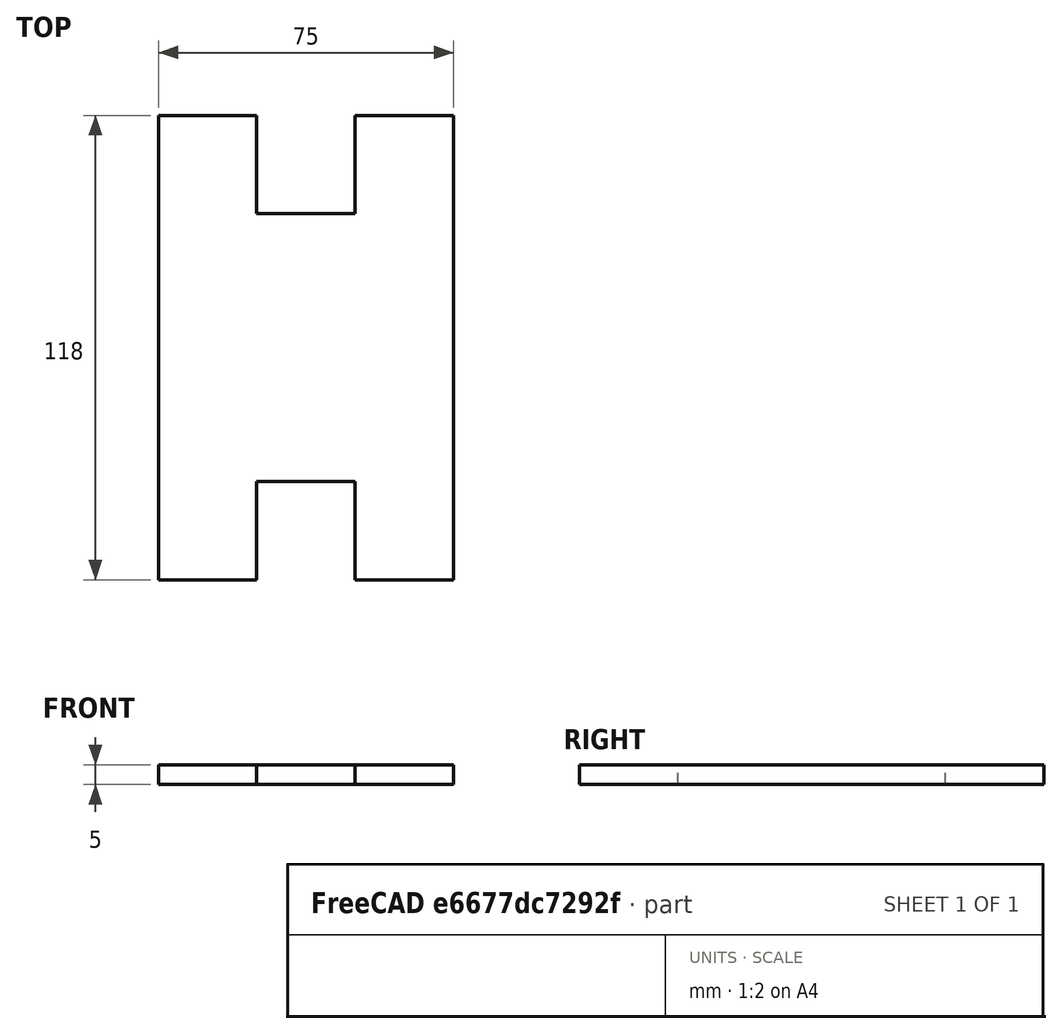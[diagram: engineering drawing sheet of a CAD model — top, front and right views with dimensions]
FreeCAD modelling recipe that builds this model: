
FCSTD DOCUMENT  (FreeCAD 0.16R5231 (Git))
Label: StepperBase
License: All rights reserved
LicenseURL: http://de.wikipedia.org/wiki/Alle_Rechte_vorbehalten
objects: Sketcher::SketchObject×1, PartDesign::Pad×1
note: 3 computed .brp shape members not serialized (recipe doc carries the construction recipe); baked Part::Feature solids carry a one-line shape summary decoded from their .brp

FEATURE [Sketcher::SketchObject] Sketch
  sketch-geometry (15):
    g0: LineSegment StartX=0 StartY=0 StartZ=0 EndX=25 EndY=0 EndZ=0
    g1: LineSegment StartX=25 StartY=0 StartZ=0 EndX=25 EndY=25 EndZ=0
    g2: LineSegment StartX=25 StartY=25 StartZ=0 EndX=50 EndY=25 EndZ=0
    g3: LineSegment StartX=50 StartY=25 StartZ=0 EndX=50 EndY=0 EndZ=0
    g4: LineSegment StartX=50 StartY=0 StartZ=0 EndX=75 EndY=0 EndZ=0
    g5: LineSegment StartX=75 StartY=0 StartZ=0 EndX=75 EndY=118 EndZ=0
    g6: LineSegment StartX=75 StartY=118 StartZ=0 EndX=50 EndY=118 EndZ=0
    g7: LineSegment StartX=50 StartY=118 StartZ=0 EndX=50 EndY=93 EndZ=0
    g8: LineSegment StartX=50 StartY=93 StartZ=0 EndX=25 EndY=93 EndZ=0
    g9: LineSegment StartX=25 StartY=93 StartZ=0 EndX=25 EndY=118 EndZ=0
    g10: LineSegment StartX=25 StartY=118 StartZ=0 EndX=0 EndY=118 EndZ=0
    g11: LineSegment StartX=0 StartY=118 StartZ=0 EndX=0 EndY=0 EndZ=0
    g12: LineSegment [constr] StartX=25 StartY=118 StartZ=0 EndX=50 EndY=118 EndZ=0
    g13: LineSegment [constr] StartX=25 StartY=93 StartZ=0 EndX=25 EndY=25 EndZ=0
    g14: LineSegment [constr] StartX=50 StartY=93 StartZ=0 EndX=50 EndY=25 EndZ=0
  constraints (41):
    c: Coincident(g-1,g0)
    c: Horizontal(g0)
    c: Coincident(g0,g1)
    c: Vertical(g1)
    c: Coincident(g1,g2)
    c: Horizontal(g2)
    c: Coincident(g2,g3)
    c: Vertical(g3)
    c: Coincident(g3,g4)
    c: Horizontal(g4)
    c: Coincident(g4,g5)
    c: Vertical(g5)
    c: Coincident(g5,g6)
    c: Horizontal(g6)
    c: Coincident(g6,g7)
    c: Vertical(g7)
    c: Coincident(g7,g8)
    c: Horizontal(g8)
    c: Coincident(g8,g9)
    c: Vertical(g9)
    c: Coincident(g9,g10)
    c: Horizontal(g10)
    c: Coincident(g10,g11)
    c: Coincident(g11,g0)
    c: Vertical(g11)
    c: PointOnObject(g3,g-1)
    c: Coincident(g12,g9)
    c: Coincident(g12,g6)
    c: Horizontal(g12)
    c: Coincident(g13,g8)
    c: Coincident(g13,g1)
    c: Coincident(g14,g7)
    c: Coincident(g14,g2)
    c: Vertical(g13)
    c: Vertical(g14)
    c: DistanceY(g-1,g10) = 118
    c: DistanceX(g0) = 25
    c: Equal(g0,g1)
    c: Equal(g1,g2)
    c: Equal(g2,g9)
    c: Equal(g9,g4)
FEATURE [PartDesign::Pad] Pad
  Length = 5
  Length2 = 100
  Sketch = -> Sketch
  Type = 0
